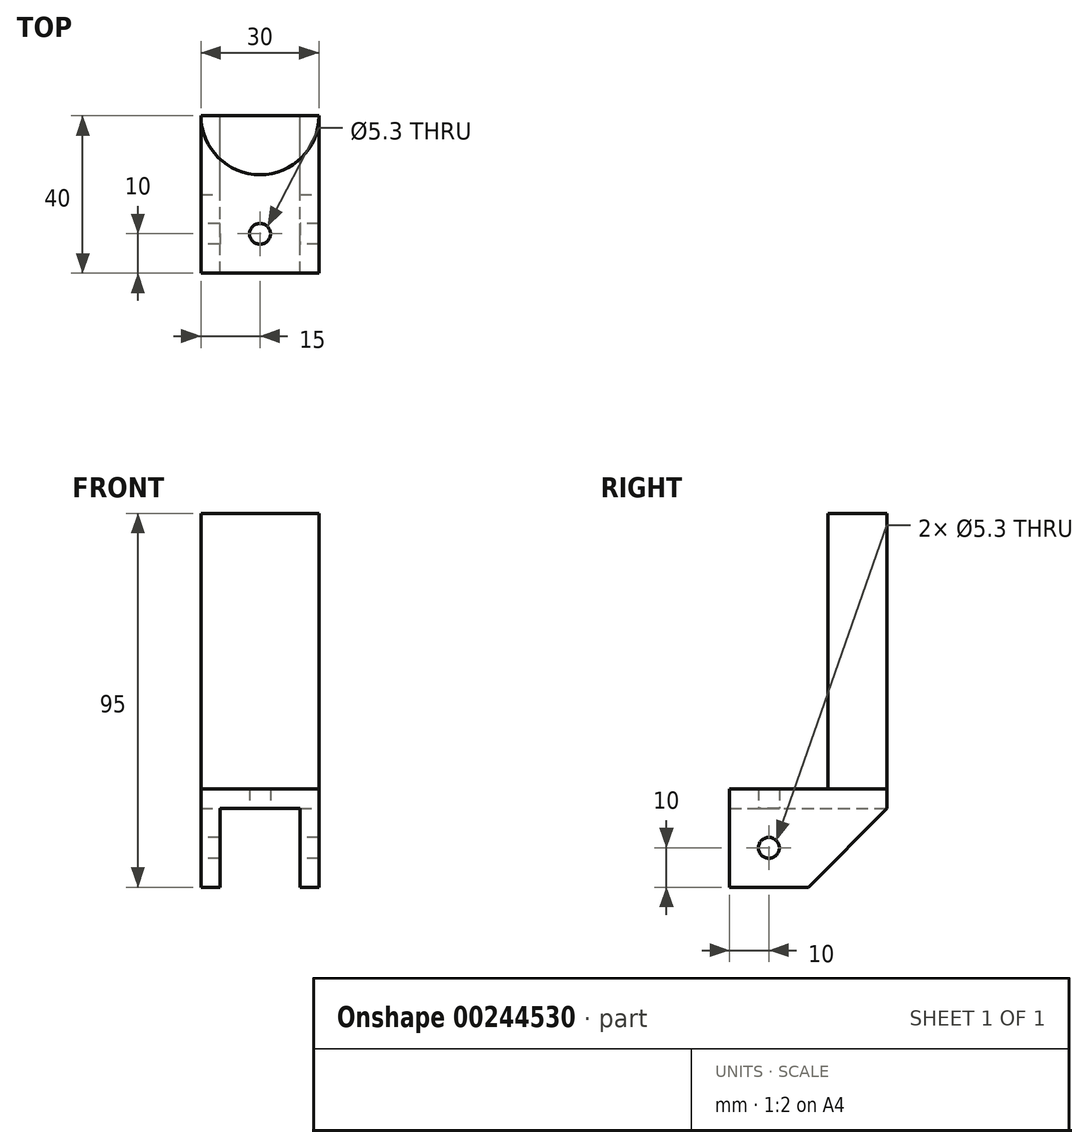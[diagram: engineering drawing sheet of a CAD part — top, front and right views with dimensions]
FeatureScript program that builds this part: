
annotation { "Feature Type Name" : "Feature", "Feature Type Description" : "" }
export const myFeature = defineFeature(function(context is Context, id is Id, definition is map)
    precondition{}
    {
        {
            var Q0;
            Q0=qCreatedBy(makeId("Top.planeOp"),FACE);
            var sketch = newSketch(context, id + "F0", { "sketchPlane" : qUnion([Q0])});
            skArc(sketch, "E0", {"start": v(-15, 0) * mm, "mid": v(0, -15) * mm, "end": v(15, 0) * mm});
            skLineSegment(sketch, "E1", {"start": v(-15, 0) * mm, "end": v(15, 0) * mm});
            skSolve(sketch);
        }
        {
            var Q0;
            Q0 = qSketchRegion(id + "F0", true);
            extrude(context, id + "F1", {"entities" : qUnion([Q0]), "depth" : 75 * mm});
        }
        {
            var Q0;
            Q0=qCreatedBy(makeId("Top.planeOp"),FACE);
            var sketch = newSketch(context, id + "F2", { "sketchPlane" : qUnion([Q0])});
            skLineSegment(sketch, "E2.bottom", {"start": v(-15, 0) * mm, "end": v(15, 0) * mm});
            skLineSegment(sketch, "E2.top", {"start": v(-15, -40) * mm, "end": v(15, -40) * mm});
            skLineSegment(sketch, "E2.left", {"start": v(-15, 0) * mm, "end": v(-15, -40) * mm});
            skLineSegment(sketch, "E2.right", {"start": v(15, 0) * mm, "end": v(15, -40) * mm});
            skCircle(sketch, "E3", {"center": v(0, -30) * mm, "radius": 2.65 * mm});
            skSolve(sketch);
        }
        {
            var Q0;
            Q0 = qSketchRegion(id + "F2", true);
            extrude(context, id + "F3", {"entities" : qUnion([Q0]), "operationType" : NewBodyOperationType.ADD, "depth" : 5 * mm});
        }
        {
            var Q0;
            Q0=makeQuery(id+"F3.boolean.opBoolean","MERGE",FACE,{"derivedFrom":[makeQuery(id+"F1.opExtrude","CAP_FACE",FACE,{"disambiguationData":[OSD([sQuery(id+"F0.wireOp",EDGE,"E0"),sQuery(id+"F0.wireOp",EDGE,"E1")])],"isStart":true}),makeQuery(id+"F3.opExtrude","CAP_FACE",FACE,{"disambiguationData":[OSD([sQuery(id+"F2.wireOp",EDGE,"E2.bottom"),sQuery(id+"F2.wireOp",EDGE,"E2.top"),sQuery(id+"F2.wireOp",EDGE,"E2.left"),sQuery(id+"F2.wireOp",EDGE,"E2.right"),sQuery(id+"F2.wireOp",EDGE,"E3")])],"isStart":true})]});
            var sketch = newSketch(context, id + "F4", { "sketchPlane" : qUnion([Q0])});
            skLineSegment(sketch, "E4.bottom", {"start": v(-15, 40) * mm, "end": v(-10.15, 40) * mm});
            skLineSegment(sketch, "E4.top", {"start": v(-15, 0) * mm, "end": v(-10.15, 0) * mm});
            skLineSegment(sketch, "E4.left", {"start": v(-15, 40) * mm, "end": v(-15, 0) * mm});
            skLineSegment(sketch, "E4.right", {"start": v(-10.15, 40) * mm, "end": v(-10.15, 0) * mm});
            skLineSegment(sketch, "E5.bottom", {"start": v(15, 40) * mm, "end": v(10.15, 40) * mm});
            skLineSegment(sketch, "E5.top", {"start": v(15, 0) * mm, "end": v(10.15, 0) * mm});
            skLineSegment(sketch, "E5.left", {"start": v(15, 40) * mm, "end": v(15, 0) * mm});
            skLineSegment(sketch, "E5.right", {"start": v(10.15, 40) * mm, "end": v(10.15, 0) * mm});
            skSolve(sketch);
        }
        {
            var Q0;
            Q0 = qSketchRegion(id + "F4", true);
            extrude(context, id + "F5", {"entities" : qUnion([Q0]), "operationType" : NewBodyOperationType.ADD, "depth" : 20 * mm});
        }
        {
            var Q0;
            Q0=makeQuery(id+"F5.boolean.opBoolean","MERGE",FACE,{"derivedFrom":[makeQuery(id+"F3.opExtrude","SWEPT_FACE",FACE,{"disambiguationData":[OSD([sQuery(id+"F2.wireOp",EDGE,"E2.left")])]}),makeQuery(id+"F5.opExtrude","SWEPT_FACE",FACE,{"disambiguationData":[OSD([sQuery(id+"F4.wireOp",EDGE,"E4.left")])]})]});
            var sketch = newSketch(context, id + "F6", { "sketchPlane" : qUnion([Q0])});
            skLineSegment(sketch, "E6.0.0", {"start": v(0, 0) * mm, "end": v(40, 0) * mm, "construction": true});
            skLineSegment(sketch, "E6.0.2", {"start": v(40, 0) * mm, "end": v(0, 0) * mm, "construction": true});
            skCircle(sketch, "E7", {"center": v(30, -10) * mm, "radius": 2.65 * mm});
            skLineSegment(sketch, "E8.0", {"start": v(27.35, 5) * mm, "end": v(32.65, 5) * mm, "construction": true});
            skSolve(sketch);
        }
        {
            var Q0;
            Q0 = qSketchRegion(id + "F6", true);
            var Q1;
            Q1=makeQuery(id+"F5.boolean.opBoolean","MERGE",FACE,{"derivedFrom":[makeQuery(id+"F3.opExtrude","SWEPT_FACE",FACE,{"disambiguationData":[OSD([sQuery(id+"F2.wireOp",EDGE,"E2.right")])]}),makeQuery(id+"F5.opExtrude","SWEPT_FACE",FACE,{"disambiguationData":[OSD([sQuery(id+"F4.wireOp",EDGE,"E5.left")])]})]});
            extrude(context, id + "F7", {"entities" : qUnion([Q0]), "operationType" : NewBodyOperationType.REMOVE, "endBound" : BoundingType.UP_TO_SURFACE, "oppositeDirection" : true, "endBoundEntityFace" : qUnion([Q1]), "depth" : 25 * mm});
        }
        {
            var Q0;
            Q0=makeQuery(id+"F5.boolean.opBoolean","MERGE",FACE,{"derivedFrom":[makeQuery(id+"F3.opExtrude","SWEPT_FACE",FACE,{"disambiguationData":[OSD([sQuery(id+"F2.wireOp",EDGE,"E2.right")])]}),makeQuery(id+"F5.opExtrude","SWEPT_FACE",FACE,{"disambiguationData":[OSD([sQuery(id+"F4.wireOp",EDGE,"E5.left")])]})]});
            var sketch = newSketch(context, id + "F8", { "sketchPlane" : qUnion([Q0])});
            skLineSegment(sketch, "E9", {"start": v(-20, -20) * mm, "end": v(0, 0) * mm});
            skLineSegment(sketch, "E10", {"start": v(0, 0) * mm, "end": v(0, -20) * mm});
            skLineSegment(sketch, "E11", {"start": v(0, -20) * mm, "end": v(-20, -20) * mm});
            skSolve(sketch);
        }
        {
            var Q0;
            Q0 = qSketchRegion(id + "F8", true);
            var Q1;
            Q1=makeQuery(id+"F5.boolean.opBoolean","MERGE",FACE,{"derivedFrom":[makeQuery(id+"F3.opExtrude","SWEPT_FACE",FACE,{"disambiguationData":[OSD([sQuery(id+"F2.wireOp",EDGE,"E2.left")])]}),makeQuery(id+"F5.opExtrude","SWEPT_FACE",FACE,{"disambiguationData":[OSD([sQuery(id+"F4.wireOp",EDGE,"E4.left")])]})]});
            extrude(context, id + "F9", {"entities" : qUnion([Q0]), "operationType" : NewBodyOperationType.REMOVE, "endBound" : BoundingType.UP_TO_SURFACE, "oppositeDirection" : true, "endBoundEntityFace" : qUnion([Q1]), "depth" : 25 * mm});
        }
    });
